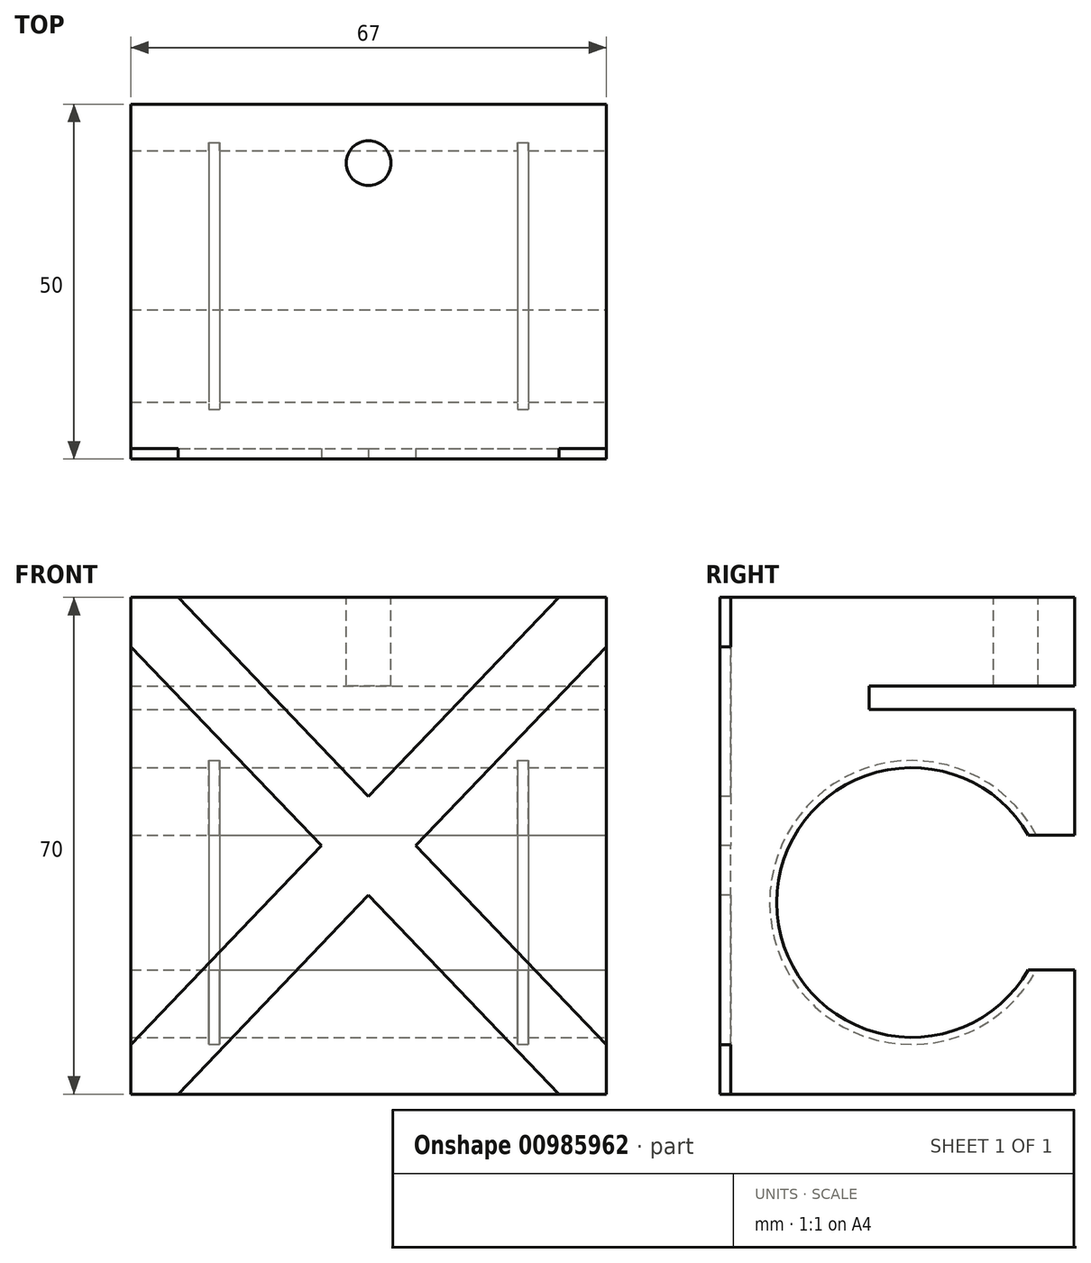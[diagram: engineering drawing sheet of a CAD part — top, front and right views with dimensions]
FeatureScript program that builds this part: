
annotation { "Feature Type Name" : "Feature", "Feature Type Description" : "" }
export const myFeature = defineFeature(function(context is Context, id is Id, definition is map)
    precondition{}
    {
        {
            var Q0;
            Q0=qCreatedBy(makeId("Top.planeOp"),FACE);
            var sketch = newSketch(context, id + "F0", { "sketchPlane" : qUnion([Q0])});
            skLineSegment(sketch, "E0.bottom", {"start": v(0, 0) * mm, "end": v(67, 0) * mm});
            skLineSegment(sketch, "E0.top", {"start": v(0, 50) * mm, "end": v(67, 50) * mm});
            skLineSegment(sketch, "E0.left", {"start": v(0, 0) * mm, "end": v(0, 50) * mm});
            skLineSegment(sketch, "E0.right", {"start": v(67, 0) * mm, "end": v(67, 50) * mm});
            skSolve(sketch);
        }
        {
            var Q0;
            Q0 = qSketchRegion(id + "F0", true);
            var Q1;
            Q1=makeQuery(id+"F0.imprint","IMPRINT",FACE,{"disambiguationData":[TD([[makeQuery(id+"F0.imprint","IMPRINT",EDGE,{"derivedFrom":sQuery(id+"F0.wireOp",EDGE,"E0.bottom")}),1.0]])]});
            extrude(context, id + "F1", {"entities" : qUnion([Q0, Q1]), "depth" : 70 * mm, "offsetDistance" : 25 * mm});
        }
        {
            var Q0;
            Q0=makeQuery(id+"F1.opExtrude","SWEPT_FACE",FACE,{"disambiguationData":[OSD([sQuery(id+"F0.wireOp",EDGE,"E0.right")])]});
            var sketch = newSketch(context, id + "F2", { "sketchPlane" : qUnion([Q0])});
            skLineSegment(sketch, "E1.bottom", {"start": v(0, 70) * mm, "end": v(50, 70) * mm});
            skLineSegment(sketch, "E1.top", {"start": v(0, 0) * mm, "end": v(50, 0) * mm});
            skLineSegment(sketch, "E1.left", {"start": v(0, 70) * mm, "end": v(0, 0) * mm});
            skLineSegment(sketch, "E1.right", {"start": v(50, 70) * mm, "end": v(50, 0) * mm});
            skLineSegment(sketch, "E2.bottom", {"start": v(50, 54.2) * mm, "end": v(21, 54.2) * mm});
            skLineSegment(sketch, "E2.top", {"start": v(50, 57.5) * mm, "end": v(21, 57.5) * mm});
            skLineSegment(sketch, "E2.left", {"start": v(50, 54.2) * mm, "end": v(50, 57.5) * mm});
            skLineSegment(sketch, "E2.right", {"start": v(21, 54.2) * mm, "end": v(21, 57.5) * mm});
            skSolve(sketch);
        }
        {
            var Q0;
            Q0=makeQuery(id+"F2.imprint","IMPRINT",FACE,{"disambiguationData":[TD([[makeQuery(id+"F2.imprint","IMPRINT",EDGE,{"derivedFrom":sQuery(id+"F2.wireOp",EDGE,"E2.bottom")}),-1.0]])]});
            extrude(context, id + "F3", {"entities" : qUnion([Q0]), "operationType" : NewBodyOperationType.REMOVE, "endBound" : BoundingType.THROUGH_ALL, "oppositeDirection" : true, "depth" : 25 * mm, "offsetDistance" : 25 * mm});
        }
        {
            var Q0;
            Q0=makeQuery(id+"F1.opExtrude","CAP_FACE",FACE,{"disambiguationData":[OSD([sQuery(id+"F0.wireOp",EDGE,"E0.bottom"),sQuery(id+"F0.wireOp",EDGE,"E0.top"),sQuery(id+"F0.wireOp",EDGE,"E0.left"),sQuery(id+"F0.wireOp",EDGE,"E0.right")])],"isStart":false});
            var sketch = newSketch(context, id + "F4", { "sketchPlane" : qUnion([Q0])});
            skCircle(sketch, "E3", {"center": v(33.5, 41.7) * mm, "radius": 3.15 * mm});
            skSolve(sketch);
        }
        {
            var Q0;
            Q0 = qSketchRegion(id + "F4", true);
            var Q1;
            Q1=makeQuery(id+"F3.boolean.opBoolean","COPY",FACE,{"derivedFrom":makeQuery(id+"F3.opExtrude","SWEPT_FACE",FACE,{"disambiguationData":[OSD([sQuery(id+"F2.wireOp",EDGE,"E2.top")])]})});
            extrude(context, id + "F5", {"entities" : qUnion([Q0]), "operationType" : NewBodyOperationType.REMOVE, "endBound" : BoundingType.UP_TO_SURFACE, "oppositeDirection" : true, "depth" : 25 * mm, "endBoundEntityFace" : qUnion([Q1]), "offsetDistance" : 25 * mm});
        }
        {
            var Q0;
            Q0=makeQuery(id+"F1.opExtrude","SWEPT_FACE",FACE,{"disambiguationData":[OSD([sQuery(id+"F0.wireOp",EDGE,"E0.bottom")])]});
            var sketch = newSketch(context, id + "F6", { "sketchPlane" : qUnion([Q0])});
            skLineSegment(sketch, "E4", {"start": v(0, 0) * mm, "end": v(67, 70) * mm});
            skLineSegment(sketch, "E5", {"start": v(0, 70) * mm, "end": v(67, 0) * mm});
            skLineSegment(sketch, "E6.0", {"start": v(0, 63.06) * mm, "end": v(60.36, 0) * mm});
            skLineSegment(sketch, "E7.0", {"start": v(6.64, 70) * mm, "end": v(67, 6.94) * mm});
            skLineSegment(sketch, "E8.0", {"start": v(6.64, 0) * mm, "end": v(67, 63.06) * mm});
            skLineSegment(sketch, "E9.0", {"start": v(0, 6.94) * mm, "end": v(60.36, 70) * mm});
            skLineSegment(sketch, "E10.bottom", {"start": v(0, 70) * mm, "end": v(6.64, 70) * mm});
            skLineSegment(sketch, "E10.top", {"start": v(0, 0) * mm, "end": v(6.64, 0) * mm});
            skLineSegment(sketch, "E10.left", {"start": v(0, 70) * mm, "end": v(0, 63.06) * mm});
            skLineSegment(sketch, "E10.right", {"start": v(67, 70) * mm, "end": v(67, 63.06) * mm});
            skLineSegment(sketch, "E11.trimOffspring", {"start": v(0, 6.94) * mm, "end": v(0, 0) * mm});
            skLineSegment(sketch, "E12.trimOffspring", {"start": v(60.36, 70) * mm, "end": v(67, 70) * mm});
            skLineSegment(sketch, "E13.trimOffspring", {"start": v(67, 6.94) * mm, "end": v(67, 0) * mm});
            skLineSegment(sketch, "E14.trimOffspring", {"start": v(60.36, 0) * mm, "end": v(67, 0) * mm});
            skSolve(sketch);
        }
        {
            var Q0;
            Q0 = qSketchRegion(id + "F6", true);
            extrude(context, id + "F7", {"entities" : qUnion([Q0]), "operationType" : NewBodyOperationType.REMOVE, "oppositeDirection" : true, "depth" : 1.5 * mm, "offsetDistance" : 25 * mm});
        }
        {
            var Q0;
            Q0=makeQuery(id+"F1.opExtrude","SWEPT_FACE",FACE,{"disambiguationData":[OSD([sQuery(id+"F0.wireOp",EDGE,"E0.right")])]});
            var sketch = newSketch(context, id + "F8", { "sketchPlane" : qUnion([Q0])});
            skCircle(sketch, "E15", {"center": v(27, 27) * mm, "radius": 19 * mm});
            skLineSegment(sketch, "E16", {"start": v(27, 27) * mm, "end": v(50, 27) * mm});
            skLineSegment(sketch, "E17.bottom", {"start": v(50, 36.5) * mm, "end": v(10.55, 36.5) * mm});
            skLineSegment(sketch, "E17.top", {"start": v(50, 17.5) * mm, "end": v(10.55, 17.5) * mm});
            skLineSegment(sketch, "E17.left", {"start": v(50, 36.5) * mm, "end": v(50, 17.5) * mm});
            skSolve(sketch);
        }
        {
            var Q0;
            Q0 = qSketchRegion(id + "F8", true);
            extrude(context, id + "F9", {"entities" : qUnion([Q0]), "operationType" : NewBodyOperationType.REMOVE, "endBound" : BoundingType.THROUGH_ALL, "oppositeDirection" : true, "depth" : 25 * mm, "offsetDistance" : 25 * mm});
        }
        {
            var Q0;
            Q0=makeQuery(id+"F1.opExtrude","SWEPT_FACE",FACE,{"disambiguationData":[OSD([sQuery(id+"F0.wireOp",EDGE,"E0.right")])]});
            cPlane(context, id + "F10", {"entities" : qUnion([Q0]), "cplaneType" : CPlaneType.OFFSET, "offset" : 11 * mm, "oppositeDirection" : true, "width" : 150 * mm, "height" : 150 * mm});
        }
        {
            var Q0;
            Q0=qCreatedBy(id+"F10.planeOp",FACE);
            var sketch = newSketch(context, id + "F11", { "sketchPlane" : qUnion([Q0])});
            skCircle(sketch, "E18", {"center": v(27, 27) * mm, "radius": 20 * mm});
            skSolve(sketch);
        }
        {
            var Q0;
            Q0 = qSketchRegion(id + "F11", true);
            extrude(context, id + "F12", {"entities" : qUnion([Q0]), "operationType" : NewBodyOperationType.REMOVE, "oppositeDirection" : true, "depth" : 1.5 * mm, "offsetDistance" : 25 * mm});
        }
        {
            var Q0;
            Q0=makeQuery(id+"F12.boolean.opBoolean","COPY",FACE,{"derivedFrom":makeQuery(id+"F12.opExtrude","CAP_FACE",FACE,{"disambiguationData":[OSD([sQuery(id+"F11.wireOp",EDGE,"E18")])],"isStart":false})});
            cPlane(context, id + "F13", {"entities" : qUnion([Q0]), "cplaneType" : CPlaneType.OFFSET, "offset" : 42 * mm, "oppositeDirection" : true, "width" : 150 * mm, "height" : 150 * mm});
        }
        {
            var Q0;
            Q0=qCreatedBy(id+"F13.planeOp",FACE);
            var sketch = newSketch(context, id + "F14", { "sketchPlane" : qUnion([Q0])});
            skCircle(sketch, "E19", {"center": v(27, 27) * mm, "radius": 20 * mm});
            skSolve(sketch);
        }
        {
            var Q0;
            Q0 = qSketchRegion(id + "F14", true);
            extrude(context, id + "F15", {"entities" : qUnion([Q0]), "operationType" : NewBodyOperationType.REMOVE, "oppositeDirection" : true, "depth" : 1.5 * mm, "offsetDistance" : 25 * mm});
        }
    });
